# Revit family: 306_bbb0ee6b22594226a4dbf83e4a22eb
name_source: partatom
category: Pipe Accessories
units: mm (PartAtom-declared; Revit-internal decimal feet)

## family parameters
Always vertical = Yes
Cut with Voids When Loaded = No
Part Type = Valve - Breaks Into
Round Connector Dimension = Use Diameter
Shared = No
Work Plane-Based = No

## types (2) — shared parameters
Description = 3-way change-over zone valve, Internal thread
H1 = 3 mm  [stored 0.00984252 ft]
H1__ve = -3 mm  [stored -0.00984252 ft]
H2 = 4 mm  [stored 0.0131234 ft]
H2__ve = -4 mm  [stored -0.0131234 ft]
H3 = 3 mm  [stored 0.00984252 ft]
L1 = 14 mm  [stored 0.0459318 ft]
L1__ve = -14 mm  [stored -0.0459318 ft]
L2D = 58 mm  [stored 0.190289 ft]
L2D_Min = 3048 mm  [stored 10 ft]
Manufacturer = Belimo
QmdConnectorList = 301;D;302;D
R2 = 6 mm  [stored 0.019685 ft]
R3 = 4 mm  [stored 0.0131234 ft]
W2D = 15 mm  [stored 0.0492126 ft]
magiPartTypeId = 306
magiProductFamilyId = bbb0ee6b22594226a4dbf83e4a22eb

## per-type parameters (varying)
| type | CenSd_H_6 | D | H | H4 | L2 | L3 | L3__ve | LL | M | R1 | magiProductId |
| C315Q-H | 13 mm | 15 mm | 15 mm  [stored 0.0492126 ft] | 18 mm  [stored 0.0590551 ft] | 23 mm | 7 mm  [stored 0.0229659 ft] | -7 mm | 29 mm  [stored 0.0951444 ft] | 32 mm  [stored 0.104987 ft] | 12 mm  [stored 0.0393701 ft] | 7cf5a9024e55402b94a37ff11ff042 |
| C320Q-J | 14 mm  [stored 0.0459318 ft] | 20 mm | 17 mm | 22 mm  [stored 0.0721785 ft] | 28 mm  [stored 0.0918635 ft] | 14 mm  [stored 0.0459318 ft] | -14 mm  [stored -0.0459318 ft] | 35 mm  [stored 0.114829 ft] | 36 mm  [stored 0.11811 ft] | 14 mm  [stored 0.0459318 ft] | 46d95ccb2263436c895b41ae1eaa0f |

note: column(s) folded — value = type name in every type: MC Product Code

note: [stored X ft] marks values corroborated as IEEE doubles in the binary element streams (Revit-internal decimal feet)

## geometry (parser evidence)
native form markers: Blend x2, Sweep x3
no freeform markers — native parametric forms only
